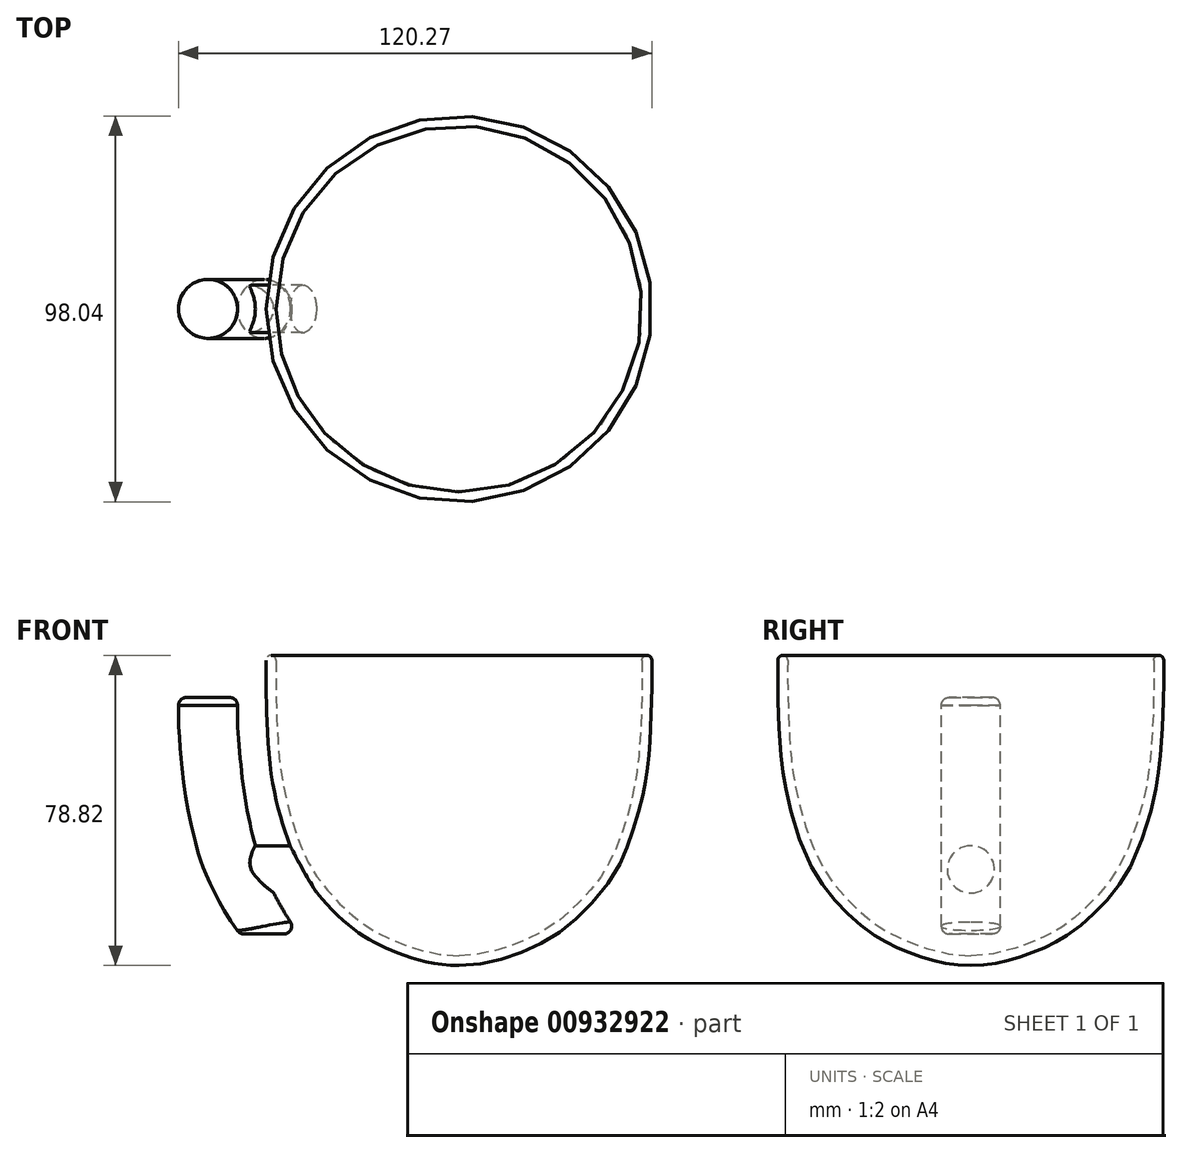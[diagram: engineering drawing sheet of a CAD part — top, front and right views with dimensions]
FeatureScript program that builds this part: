
annotation { "Feature Type Name" : "Feature", "Feature Type Description" : "" }
export const myFeature = defineFeature(function(context is Context, id is Id, definition is map)
    precondition{}
    {
        {
            var Q0;
            Q0=qCreatedBy(makeId("Front.planeOp"),FACE);
            var sketch = newSketch(context, id + "F0", { "sketchPlane" : qUnion([Q0])});
            skLineSegment(sketch, "E0", {"start": v(0, 78.82) * mm, "end": v(-49, 78.82) * mm});
            skLineSegment(sketch, "E1", {"start": v(0, 0) * mm, "end": v(0, 78.82) * mm});
            skFitSpline(sketch, "E2", {"points": [v(-49, 78.82) * mm, v(-49, 71.2) * mm, v(-47.95, 50.94) * mm, v(-44.24, 34.32) * mm, v(-38.54, 21.8) * mm, v(-27.37, 9.77) * mm, v(-17.3, 3.96) * mm, v(0, 0) * mm], "startDerivative": vector(-0.53, -120.05) * mm, "endDerivative": vector(126.32, 0) * mm});
            skSolve(sketch);
        }
        {
            var Q0;
            Q0=qSketchRegion(id+"F0",true);
            var Q1;
            Q1=sQuery(id+"F0.wireOp",EDGE,"E1");
            revolve(context, id + "F1", {"surfaceOperationType" : NewSurfaceOperationType.NEW, "entities" : qUnion([Q0]), "axis" : qUnion([Q1]), "revolveType" : RevolveType.FULL});
        }
        {
            var Q0;
            Q0=makeQuery(id+"F1.opRevolve","SWEPT_FACE",FACE,{"disambiguationData":[OSD([sQuery(id+"F0.wireOp",EDGE,"E0")])]});
            shell(context, id + "F2", {"entities" : qUnion([Q0]), "thickness" : 2.5 * mm});
        }
        {
            var Q0;
            Q0=makeQuery(id+"F1.opRevolve","SWEPT_EDGE",EDGE,{"disambiguationData":[OSD([sQuery(id+"F0.wireOp",EDGE,"E0"),sQuery(id+"F0.wireOp",EDGE,"E2")])]});
            var Q1;
            Q1=makeQuery(id+"F2.opShell","OFFSET_EDGE",EDGE,{"disambiguationData":[OSD([sQuery(id+"F0.wireOp",EDGE,"E0"),sQuery(id+"F0.wireOp",EDGE,"E2")])]});
            fillet(context, id + "F3", {"entities" : qUnion([Q0, Q1]), "radius" : 1.25 * mm, "tangentPropagation" : true, "defaultsChanged" : true, "vertexSettings" : [], "allowEdgeOverflow" : false});
        }
        {
            var Q0;
            Q0=qCreatedBy(makeId("Front.planeOp"),FACE);
            var sketch = newSketch(context, id + "F4", { "sketchPlane" : qUnion([Q0])});
            skLineSegment(sketch, "E3", {"start": v(-41.77, 30.38) * mm, "end": v(-53.43, 30.38) * mm});
            skLineSegment(sketch, "E4", {"start": v(-49.23, 20.12) * mm, "end": v(-36.53, 20.12) * mm});
            skLineSegment(sketch, "E5", {"start": v(-36.53, 20.12) * mm, "end": v(-41.77, 30.38) * mm});
            skFitSpline(sketch, "E6", {"points": [v(-42.03, 8) * mm, v(-47.44, 16.94) * mm, v(-49.23, 20.12) * mm, v(-51.33, 24.44) * mm, v(-53.43, 30.38) * mm, v(-55.23, 38.72) * mm, v(-56.67, 49.18) * mm, v(-57.32, 61.86) * mm, v(-57.58, 68.13) * mm, v(-57.6, 68.09) * mm], "startDerivative": vector(-47.1, 69.03) * mm, "endDerivative": vector(-6.03, -13.35) * mm});
            skLineSegment(sketch, "E7", {"start": v(-57.58, 68.13) * mm, "end": v(-69.83, 68.13) * mm});
            skFitSpline(sketch, "E8", {"points": [v(-69.83, 68.13) * mm, v(-69.83, 61.07) * mm, v(-69.06, 51.29) * mm, v(-67.63, 40.46) * mm, v(-65.54, 31.18) * mm, v(-63.64, 25) * mm, v(-58.64, 14.66) * mm, v(-54.3, 8) * mm], "startDerivative": vector(-1.12, -53.42) * mm, "endDerivative": vector(31.44, -44.67) * mm});
            skLineSegment(sketch, "E9", {"start": v(-54.3, 8) * mm, "end": v(-42.03, 8) * mm});
            skSolve(sketch);
        }
        {
            var Q0;
            Q0=qCreatedBy(makeId("Right.planeOp"),FACE);
            cPlane(context, id + "F5", {"entities" : qUnion([Q0]), "cplaneType" : CPlaneType.OFFSET, "offset" : 55 * mm, "oppositeDirection" : true, "width" : 150 * mm, "height" : 150 * mm});
        }
        {
            var Q0;
            Q0=qCreatedBy(id+"F5.planeOp",FACE);
            var sketch = newSketch(context, id + "F6", { "sketchPlane" : qUnion([Q0])});
            skPoint(sketch, "E10.middle", {"position": v(0, 24.44) * mm});
            skCircle(sketch, "E11", {"center": v(0, 24.44) * mm, "radius": 6 * mm});
            skSolve(sketch);
        }
        {
            var Q0;
            Q0=qSketchRegion(id+"F6",true);
            extrude(context, id + "F7", {"entities" : qUnion([Q0]), "operationType" : NewBodyOperationType.ADD, "endBound" : BoundingType.UP_TO_NEXT, "depth" : 25 * mm, "offsetDistance" : 25 * mm});
        }
        {
            var Q0;
            Q0=qCreatedBy(makeId("Top.planeOp"),FACE);
            cPlane(context, id + "F8", {"entities" : qUnion([Q0]), "cplaneType" : CPlaneType.OFFSET, "offset" : 8 * mm, "width" : 150 * mm, "height" : 150 * mm});
        }
        {
            var Q0;
            Q0=qCreatedBy(id+"F8.planeOp",FACE);
            var sketch = newSketch(context, id + "F9", { "sketchPlane" : qUnion([Q0])});
            skPoint(sketch, "E12.middle", {"position": v(-48.17, 0) * mm});
            skCircle(sketch, "E13", {"center": v(-48.17, 0) * mm, "radius": 7.5 * mm});
            skSolve(sketch);
        }
        {
            var Q0;
            Q0 = qSketchRegion(id + "F9", true);
            var Q1;
            Q1=sQuery(id+"F4.wireOp",EDGE,"E8");
            sweep(context, id + "F10", {"operationType" : NewBodyOperationType.ADD, "profiles" : qUnion([Q0]), "path" : qUnion([Q1]), "keepProfileOrientation" : true});
        }
        {
            var Q0;
            Q0=makeQuery(id+"F10.opSweep","CAP_FACE",FACE,{"disambiguationData":[OSD([sQuery(id+"F4.wireOp",VERTEX,"E8.start"),sQuery(id+"F9.wireOp",EDGE,"E12.bottom"),sQuery(id+"F9.wireOp",EDGE,"E12.top"),sQuery(id+"F9.wireOp",EDGE,"E12.left"),sQuery(id+"F9.wireOp",EDGE,"E12.right")])],"isStart":false});
            var Q1;
            Q1=makeQuery(id+"F10.opSweep","CAP_FACE",FACE,{"disambiguationData":[OSD([sQuery(id+"F4.wireOp",VERTEX,"E8.end"),sQuery(id+"F9.wireOp",EDGE,"E12.bottom"),sQuery(id+"F9.wireOp",EDGE,"E12.top"),sQuery(id+"F9.wireOp",EDGE,"E12.left"),sQuery(id+"F9.wireOp",EDGE,"E12.right")])],"isStart":true});
            fillet(context, id + "F11", {"entities" : qUnion([Q0, Q1]), "radius" : 2 * mm, "tangentPropagation" : true, "allowEdgeOverflow" : false});
        }
    });
